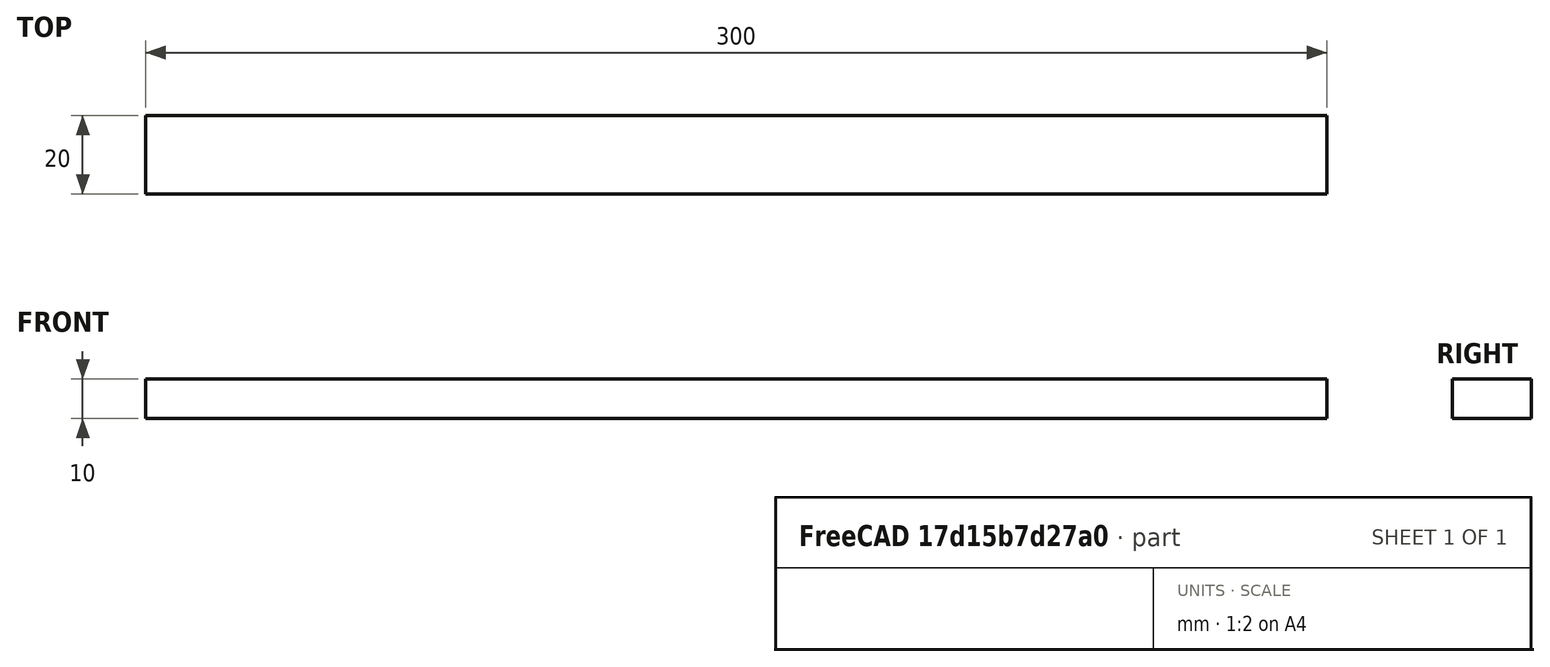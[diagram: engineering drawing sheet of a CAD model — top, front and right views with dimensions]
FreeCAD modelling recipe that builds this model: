
FCSTD DOCUMENT  (FreeCAD 0.20R29410 (Git))
Label: Bar_Minus50mm
License: All rights reserved
LicenseURL: http://en.wikipedia.org/wiki/All_rights_reserved
objects: Sketcher::SketchObject×1, PartDesign::Pad×1, PartDesign::Body×1
note: 4 computed .brp shape members not serialized (recipe doc carries the construction recipe); baked Part::Feature solids carry a one-line shape summary decoded from their .brp

FEATURE [Sketcher::SketchObject] Sketch
  FullyConstrained = true
  MapMode = 5
  Placement = pos=(0,0,0) rot=(0.57735,0.57735,0.57735;2.0944rad)
  Support = -> [YZ_Plane]
  sketch-geometry (5):
    g0: LineSegment StartX=60 StartY=5 StartZ=0 EndX=60 EndY=-5 EndZ=0
    g1: LineSegment StartX=60 StartY=-5 StartZ=0 EndX=40 EndY=-5 EndZ=0
    g2: LineSegment StartX=40 StartY=-5 StartZ=0 EndX=40 EndY=5 EndZ=0
    g3: LineSegment StartX=40 StartY=5 StartZ=0 EndX=60 EndY=5 EndZ=0
    g4: GeomPoint X=50 Y=2e-16 Z=0
  constraints (13):
    c: Coincident(g0,g1)
    c: Coincident(g1,g2)
    c: Coincident(g2,g3)
    c: Coincident(g3,g0)
    c: Horizontal(g1)
    c: Horizontal(g3)
    c: Vertical(g0)
    c: Vertical(g2)
    c: Symmetric(g1,g0,g4)
    c: DistanceY(g-1,g4) = 0
    c: DistanceX(g4,g-1) = -50
    c: DistanceX(g1,g1) = 20
    c: DistanceY(g2,g2) = 10
FEATURE [PartDesign::Pad] Pad
  Direction = (1,-2e-16,3e-16)
  Length = 300
  Length2 = 10
  Placement = pos=(0,0,0) rot=(0.57735,0.57735,0.57735;2.0944rad)
  Profile = -> Sketch
  ReferenceAxis = -> Sketch [N_Axis]
  Type = 0
FEATURE [PartDesign::Body] Body
  Group = -> [Sketch,Pad]
  Origin = -> Origin
  Tip = -> Pad
